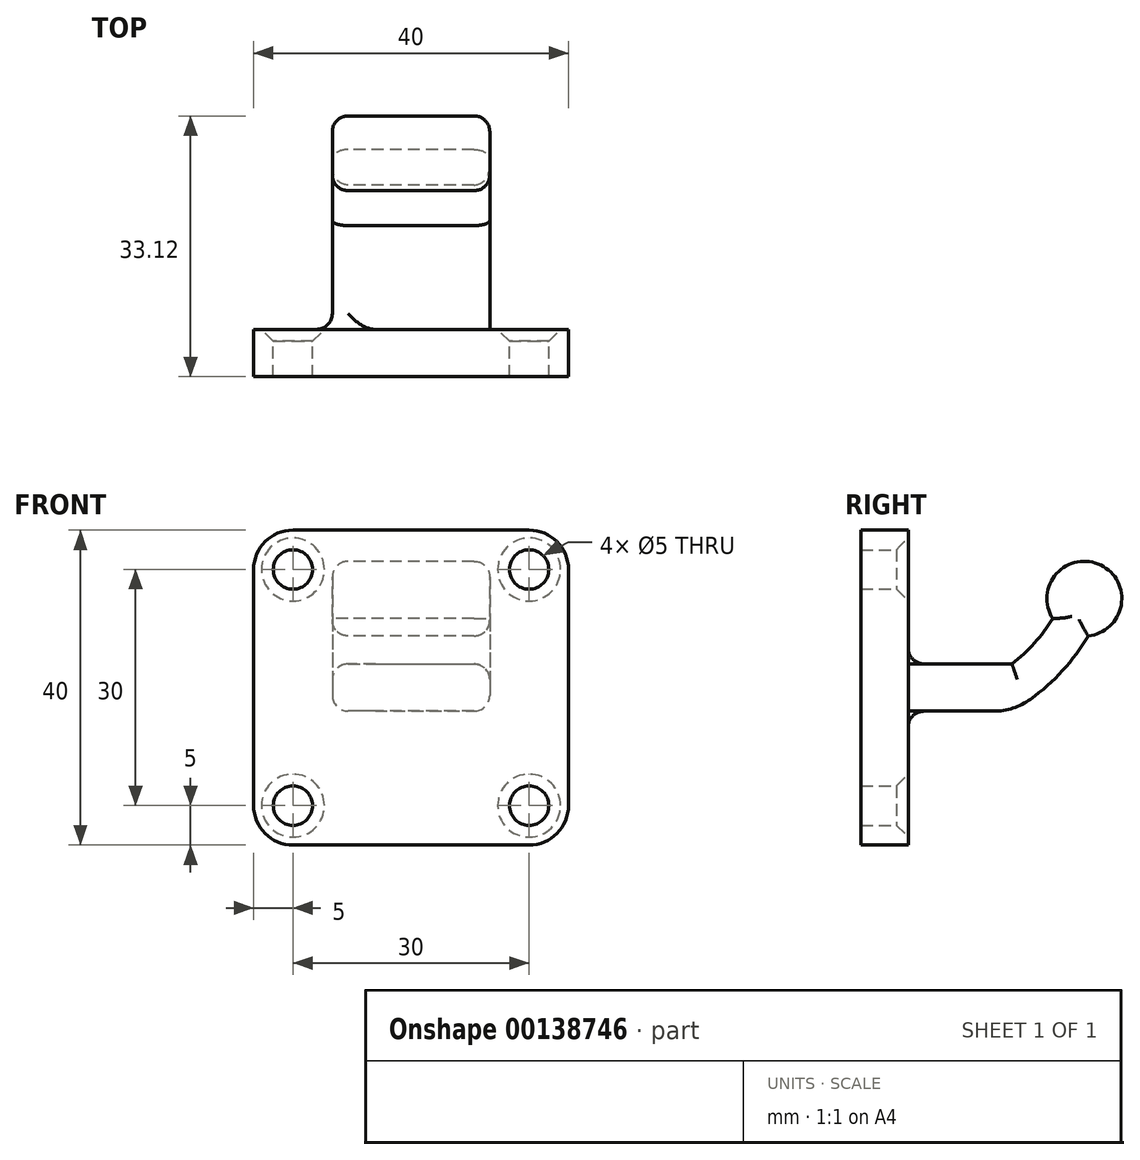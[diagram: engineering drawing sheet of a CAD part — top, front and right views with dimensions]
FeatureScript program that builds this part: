
annotation { "Feature Type Name" : "Feature", "Feature Type Description" : "" }
export const myFeature = defineFeature(function(context is Context, id is Id, definition is map)
    precondition{}
    {
        {
            var Q0;
            Q0=qCreatedBy(makeId("Front.planeOp"),FACE);
            var sketch = newSketch(context, id + "F0", { "sketchPlane" : qUnion([Q0])});
            skLineSegment(sketch, "E0.bottom", {"start": v(-5, 0) * mm, "end": v(-35, 0) * mm});
            skLineSegment(sketch, "E0.top", {"start": v(-5, 40) * mm, "end": v(-35, 40) * mm});
            skLineSegment(sketch, "E0.left", {"start": v(0, 5) * mm, "end": v(0, 35) * mm});
            skLineSegment(sketch, "E0.right", {"start": v(-40, 5) * mm, "end": v(-40, 35) * mm});
            skPoint(sketch, "E1.visualSharp", {"position": v(0, 40) * mm});
            skArc(sketch, "E1.filletArc", {"start": v(0, 35) * mm, "mid": v(-1.46, 38.54) * mm, "end": v(-5, 40) * mm});
            skPoint(sketch, "E2.visualSharp", {"position": v(0, 0) * mm});
            skArc(sketch, "E2.filletArc", {"start": v(-5, 0) * mm, "mid": v(-1.46, 1.46) * mm, "end": v(0, 5) * mm});
            skPoint(sketch, "E3.visualSharp", {"position": v(-40, 0) * mm});
            skArc(sketch, "E3.filletArc", {"start": v(-40, 5) * mm, "mid": v(-38.54, 1.46) * mm, "end": v(-35, 0) * mm});
            skPoint(sketch, "E4.visualSharp", {"position": v(-40, 40) * mm});
            skArc(sketch, "E4.filletArc", {"start": v(-35, 40) * mm, "mid": v(-38.54, 38.54) * mm, "end": v(-40, 35) * mm});
            skLineSegment(sketch, "E5", {"start": v(-20, 40) * mm, "end": v(-20, 47.25) * mm});
            skSolve(sketch);
        }
        {
            var Q0;
            Q0=makeQuery(id+"F0.imprint","IMPRINT",FACE,{"disambiguationData":[TD([[makeQuery(id+"F0.imprint","IMPRINT",EDGE,{"derivedFrom":sQuery(id+"F0.wireOp",EDGE,"E0.bottom")}),-1.0]])]});
            extrude(context, id + "F1", {"entities" : qUnion([Q0]), "depth" : 6 * mm});
        }
        {
            var Q0;
            Q0=makeQuery(id+"F1.opExtrude","CAP_FACE",FACE,{"disambiguationData":[OSD([sQuery(id+"F0.wireOp",EDGE,"E0.bottom"),sQuery(id+"F0.wireOp",EDGE,"E0.top"),sQuery(id+"F0.wireOp",EDGE,"E0.left"),sQuery(id+"F0.wireOp",EDGE,"E0.right"),sQuery(id+"F0.wireOp",EDGE,"E1.filletArc"),sQuery(id+"F0.wireOp",EDGE,"E2.filletArc"),sQuery(id+"F0.wireOp",EDGE,"E3.filletArc"),sQuery(id+"F0.wireOp",EDGE,"E4.filletArc")])],"isStart":false});
            var sketch = newSketch(context, id + "F2", { "sketchPlane" : qUnion([Q0])});
            skLineSegment(sketch, "E6", {"start": v(-20, 40) * mm, "end": v(-20, 0) * mm});
            skLineSegment(sketch, "E7", {"start": v(-40, 20) * mm, "end": v(0, 20) * mm});
            skLineSegment(sketch, "E8.bottom", {"start": v(-30, 23) * mm, "end": v(-10, 23) * mm});
            skLineSegment(sketch, "E8.top", {"start": v(-30, 17) * mm, "end": v(-10, 17) * mm});
            skLineSegment(sketch, "E8.left", {"start": v(-30, 23) * mm, "end": v(-30, 17) * mm});
            skLineSegment(sketch, "E8.right", {"start": v(-10, 23) * mm, "end": v(-10, 17) * mm});
            skPoint(sketch, "E8.middle", {"position": v(-20, 20) * mm});
            skSolve(sketch);
        }
        {
            var Q0;
            {var subQ0=sQuery(id+"F2.wireOp",EDGE,"E8.bottom");var subQ1=sQuery(id+"F2.wireOp",EDGE,"E6");var subQ2=makeQuery(id+"F2.imprint","INTERSECT",VERTEX,{"derivedFrom":[subQ1,subQ0]});Q0=makeQuery(id+"F2.imprint","IMPRINT",FACE,{"disambiguationData":[TD([[makeQuery(id+"F2.imprint","IMPRINT",EDGE,{"disambiguationData":[TD([[subQ2,-1.0]])],"derivedFrom":subQ1}),-1.0]])]});}
            var Q1;
            {var subQ0=sQuery(id+"F2.wireOp",EDGE,"E8.bottom");var subQ1=sQuery(id+"F2.wireOp",EDGE,"E6");var subQ2=makeQuery(id+"F2.imprint","INTERSECT",VERTEX,{"derivedFrom":[subQ1,subQ0]});Q1=makeQuery(id+"F2.imprint","IMPRINT",FACE,{"disambiguationData":[TD([[makeQuery(id+"F2.imprint","IMPRINT",EDGE,{"disambiguationData":[TD([[subQ2,-1.0]])],"derivedFrom":subQ1}),1.0]])]});}
            var Q2;
            {var subQ0=sQuery(id+"F2.wireOp",EDGE,"E7");var subQ1=sQuery(id+"F2.wireOp",EDGE,"E6");var subQ2=makeQuery(id+"F2.imprint","INTERSECT",VERTEX,{"derivedFrom":[subQ1,subQ0]});Q2=makeQuery(id+"F2.imprint","IMPRINT",FACE,{"disambiguationData":[TD([[makeQuery(id+"F2.imprint","IMPRINT",EDGE,{"disambiguationData":[TD([[subQ2,-1.0]])],"derivedFrom":subQ1}),1.0]])]});}
            var Q3;
            {var subQ0=sQuery(id+"F2.wireOp",EDGE,"E7");var subQ1=sQuery(id+"F2.wireOp",EDGE,"E6");var subQ2=makeQuery(id+"F2.imprint","INTERSECT",VERTEX,{"derivedFrom":[subQ1,subQ0]});Q3=makeQuery(id+"F2.imprint","IMPRINT",FACE,{"disambiguationData":[TD([[makeQuery(id+"F2.imprint","IMPRINT",EDGE,{"disambiguationData":[TD([[subQ2,-1.0]])],"derivedFrom":subQ1}),-1.0]])]});}
            extrude(context, id + "F3", {"entities" : qUnion([Q0, Q1, Q2, Q3]), "operationType" : NewBodyOperationType.ADD, "oppositeDirection" : true, "depth" : 19.18 * mm});
        }
        {
            var Q0;
            Q0=makeQuery(id+"F3.opExtrude","CAP_FACE",FACE,{"disambiguationData":[OSD([sQuery(id+"F2.wireOp",EDGE,"E8.bottom"),sQuery(id+"F2.wireOp",EDGE,"E8.top"),sQuery(id+"F2.wireOp",EDGE,"E8.left"),sQuery(id+"F2.wireOp",EDGE,"E8.right")])],"isStart":false});
            var Q1;
            Q1=sQuery(id+"F0.wireOp",EDGE,"E0.top");
            revolve(context, id + "F4", {"operationType" : NewBodyOperationType.ADD, "entities" : qUnion([Q0]), "axis" : qUnion([Q1]), "revolveType" : RevolveType.ONE_DIRECTION, "oppositeDirection" : true, "angle" : 40.97 * degree});
        }
        {
            var Q0;
            Q0=makeQuery(id+"F3.opExtrude","SWEPT_EDGE",EDGE,{"disambiguationData":[OSD([sQuery(id+"F2.wireOp",EDGE,"E8.bottom"),sQuery(id+"F2.wireOp",EDGE,"E8.right")])]});
            var Q1;
            Q1=makeQuery(id+"F4.opRevolve","SWEPT_EDGE",EDGE,{"disambiguationData":[OSD([sQuery(id+"F2.wireOp",EDGE,"E8.bottom"),sQuery(id+"F2.wireOp",EDGE,"E8.right")])]});
            var Q2;
            Q2=makeQuery(id+"F4.opRevolve","SWEPT_EDGE",EDGE,{"disambiguationData":[OSD([sQuery(id+"F2.wireOp",EDGE,"E8.top"),sQuery(id+"F2.wireOp",EDGE,"E8.right")])]});
            var Q3;
            Q3=makeQuery(id+"F3.opExtrude","SWEPT_EDGE",EDGE,{"disambiguationData":[OSD([sQuery(id+"F2.wireOp",EDGE,"E8.top"),sQuery(id+"F2.wireOp",EDGE,"E8.right")])]});
            var Q4;
            {var subQ0=sQuery(id+"F2.wireOp",EDGE,"E8.left");Q4=makeQuery(id+"F4.boolean.opBoolean","MERGE",FACE,{"derivedFrom":[makeQuery(id+"F3.opExtrude","SWEPT_FACE",FACE,{"disambiguationData":[OSD([subQ0])]}),makeQuery(id+"F4.opRevolve","SWEPT_FACE",FACE,{"disambiguationData":[OSD([subQ0])]})]});}
            fillet(context, id + "F5", {"entities" : qUnion([Q0, Q1, Q2, Q3, Q4]), "radius" : 2 * mm, "tangentPropagation" : true, "allowEdgeOverflow" : false});
        }
        {
            var Q0;
            {var subQ0=sQuery(id+"F2.wireOp",EDGE,"E8.left");Q0=makeQuery(id+"F4.boolean.opBoolean","MERGE",FACE,{"derivedFrom":[makeQuery(id+"F3.opExtrude","SWEPT_FACE",FACE,{"disambiguationData":[OSD([subQ0])]}),makeQuery(id+"F4.opRevolve","SWEPT_FACE",FACE,{"disambiguationData":[OSD([subQ0])]})]});}
            var sketch = newSketch(context, id + "F6", { "sketchPlane" : qUnion([Q0])});
            skCircle(sketch, "E9", {"center": v(-22.37, 31.29) * mm, "radius": 4.75 * mm});
            skSolve(sketch);
        }
        {
            var Q0;
            {var subQ1=sQuery(id+"F2.wireOp",EDGE,"E8.left");var subQ2=makeQuery(id+"F4.boolean.opBoolean","MERGE",FACE,{"derivedFrom":[makeQuery(id+"F3.opExtrude","SWEPT_FACE",FACE,{"disambiguationData":[OSD([subQ1])]}),makeQuery(id+"F4.opRevolve","SWEPT_FACE",FACE,{"disambiguationData":[OSD([subQ1])]})]});var subQ7=makeQuery(id+"F5.opFillet","BLEND_EDGE",EDGE,{"blendedFrom":[makeQuery(id+"F4.opRevolve","CAP_EDGE",EDGE,{"disambiguationData":[OSD([subQ1]),OD(1.0)],"isStart":false}),subQ2],"blendedInto":[subQ2]});Q0=makeQuery(id+"F6.imprint","IMPRINT",FACE,{"disambiguationData":[TD([[makeQuery(id+"F6.imprint","IMPRINT",EDGE,{"derivedFrom":subQ7}),-1.0]])]});}
            extrude(context, id + "F7", {"entities" : qUnion([Q0]), "operationType" : NewBodyOperationType.ADD, "oppositeDirection" : true, "depth" : 20 * mm});
        }
        {
            var Q0;
            Q0=makeQuery(id+"F7.opExtrude","CAP_EDGE",EDGE,{"disambiguationData":[OSD([sQuery(id+"F6.wireOp",EDGE,"E9")])],"isStart":true});
            var Q1;
            Q1=makeQuery(id+"F7.opExtrude","CAP_EDGE",EDGE,{"disambiguationData":[OSD([sQuery(id+"F6.wireOp",EDGE,"E9")])],"isStart":false});
            fillet(context, id + "F8", {"entities" : qUnion([Q0, Q1]), "radius" : 2 * mm, "tangentPropagation" : true, "allowEdgeOverflow" : false});
        }
        {
            var Q0;
            Q0=sQuery(id+"F0.wireOp",VERTEX,"E4.filletArc.center");
            var Q1;
            Q1=sQuery(id+"F0.wireOp",VERTEX,"E1.filletArc.center");
            var Q2;
            Q2=sQuery(id+"F0.wireOp",VERTEX,"E2.filletArc.center");
            var Q3;
            Q3=sQuery(id+"F0.wireOp",VERTEX,"E3.filletArc.center");
            var Q4;
            Q4=makeQuery(id+"F1.opExtrude","SWEPT_BODY",BODY,{"disambiguationData":[OSD([sQuery(id+"F0.wireOp",EDGE,"E0.bottom"),sQuery(id+"F0.wireOp",EDGE,"E0.top"),sQuery(id+"F0.wireOp",EDGE,"E0.left"),sQuery(id+"F0.wireOp",EDGE,"E0.right"),sQuery(id+"F0.wireOp",EDGE,"E1.filletArc"),sQuery(id+"F0.wireOp",EDGE,"E2.filletArc"),sQuery(id+"F0.wireOp",EDGE,"E3.filletArc"),sQuery(id+"F0.wireOp",EDGE,"E4.filletArc")])]});
            hole(context, id + "F9", {"style" : HoleStyle.C_SINK, "endStyle" : HoleEndStyle.THROUGH, "oppositeDirection" : true, "holeDiameter" : 5 * mm, "cSinkDiameter" : 8 * mm, "cSinkAngle" : 90 * degree, "startFromSketch" : true, "locations" : qUnion([Q0, Q1, Q2, Q3]), "scope" : qUnion([Q4]), "isTappedThrough" : true});
        }
        {
            var Q0;
            {var subQ0=sQuery(id+"F2.wireOp",EDGE,"E8.top");Q0=makeQuery(id+"F4.boolean.opBoolean","MERGE",EDGE,{"derivedFrom":[makeQuery(id+"F3.opExtrude","CAP_EDGE",EDGE,{"disambiguationData":[OSD([subQ0])],"isStart":false}),makeQuery(id+"F4.opRevolve","CAP_EDGE",EDGE,{"disambiguationData":[OSD([subQ0]),OD(0.0)],"isStart":false})]});}
            fillet(context, id + "F10", {"entities" : qUnion([Q0]), "radius" : 8 * mm, "tangentPropagation" : true, "allowEdgeOverflow" : false});
        }
    });
